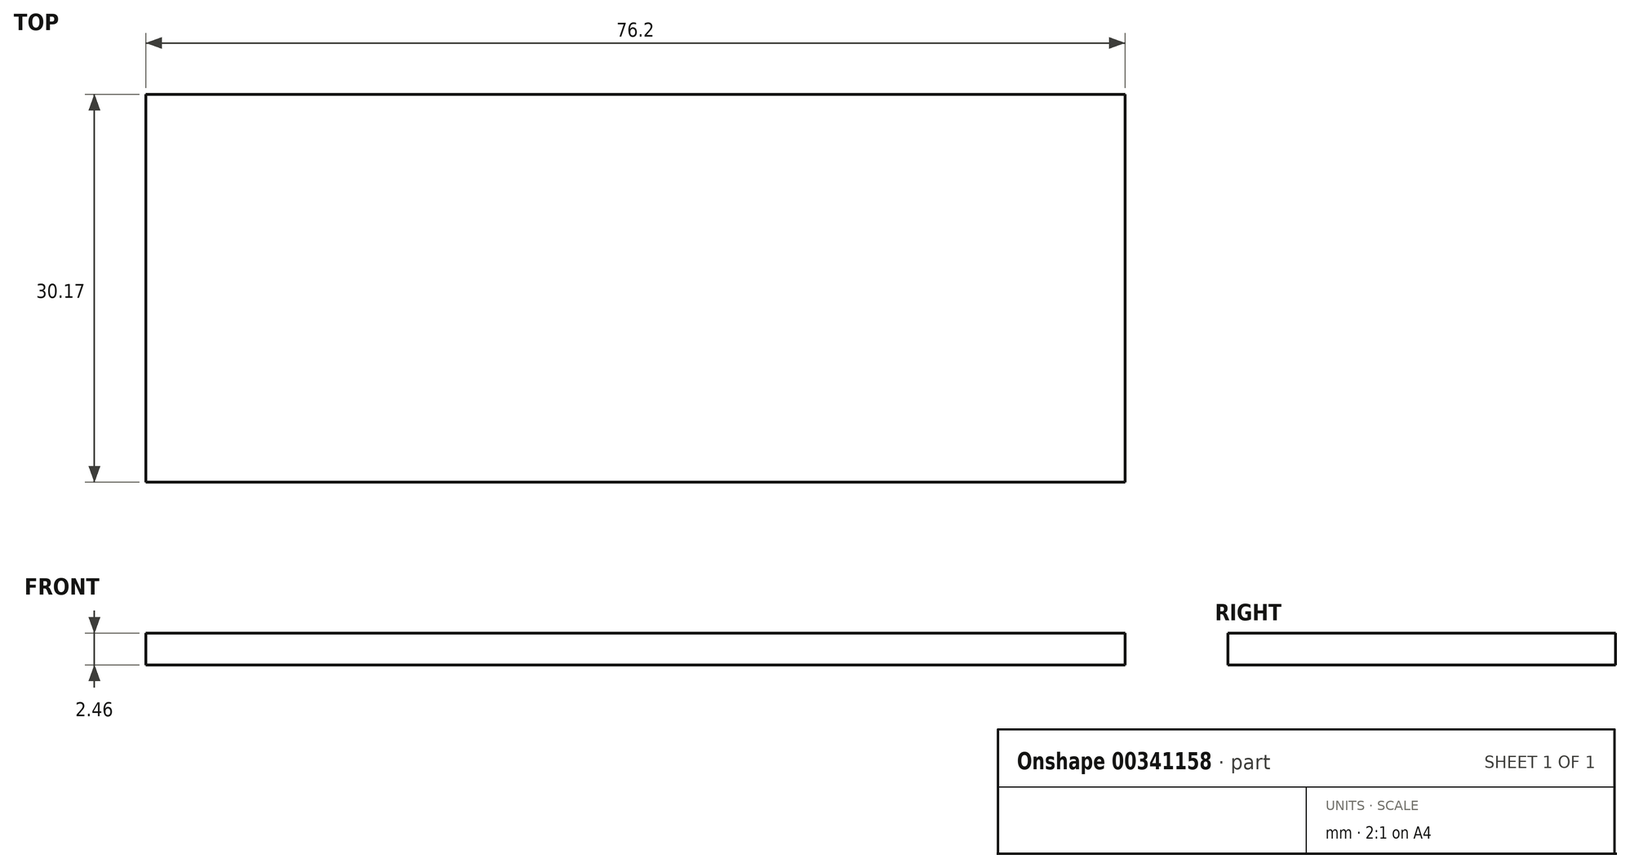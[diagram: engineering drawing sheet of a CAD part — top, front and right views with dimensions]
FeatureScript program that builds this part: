
annotation { "Feature Type Name" : "Feature", "Feature Type Description" : "" }
export const myFeature = defineFeature(function(context is Context, id is Id, definition is map)
    precondition{}
    {
        {
            var Q0;
            Q0=qCreatedBy(makeId("Top.planeOp"),FACE);
            var sketch = newSketch(context, id + "F0", { "sketchPlane" : qUnion([Q0])});
            skLineSegment(sketch, "E0.bottom", {"start": v(-15.6, -15.67) * mm, "end": v(60.6, -15.67) * mm});
            skLineSegment(sketch, "E0.top", {"start": v(-15.6, 14.5) * mm, "end": v(60.6, 14.5) * mm});
            skLineSegment(sketch, "E0.left", {"start": v(-15.6, -15.67) * mm, "end": v(-15.6, 14.5) * mm});
            skLineSegment(sketch, "E0.right", {"start": v(60.6, -15.67) * mm, "end": v(60.6, 14.5) * mm});
            skSolve(sketch);
        }
        {
            var Q0;
            Q0 = qSketchRegion(id + "F0", true);
            extrude(context, id + "F1", {"entities" : qUnion([Q0]), "depth" : 2.46 * mm});
        }
    });
